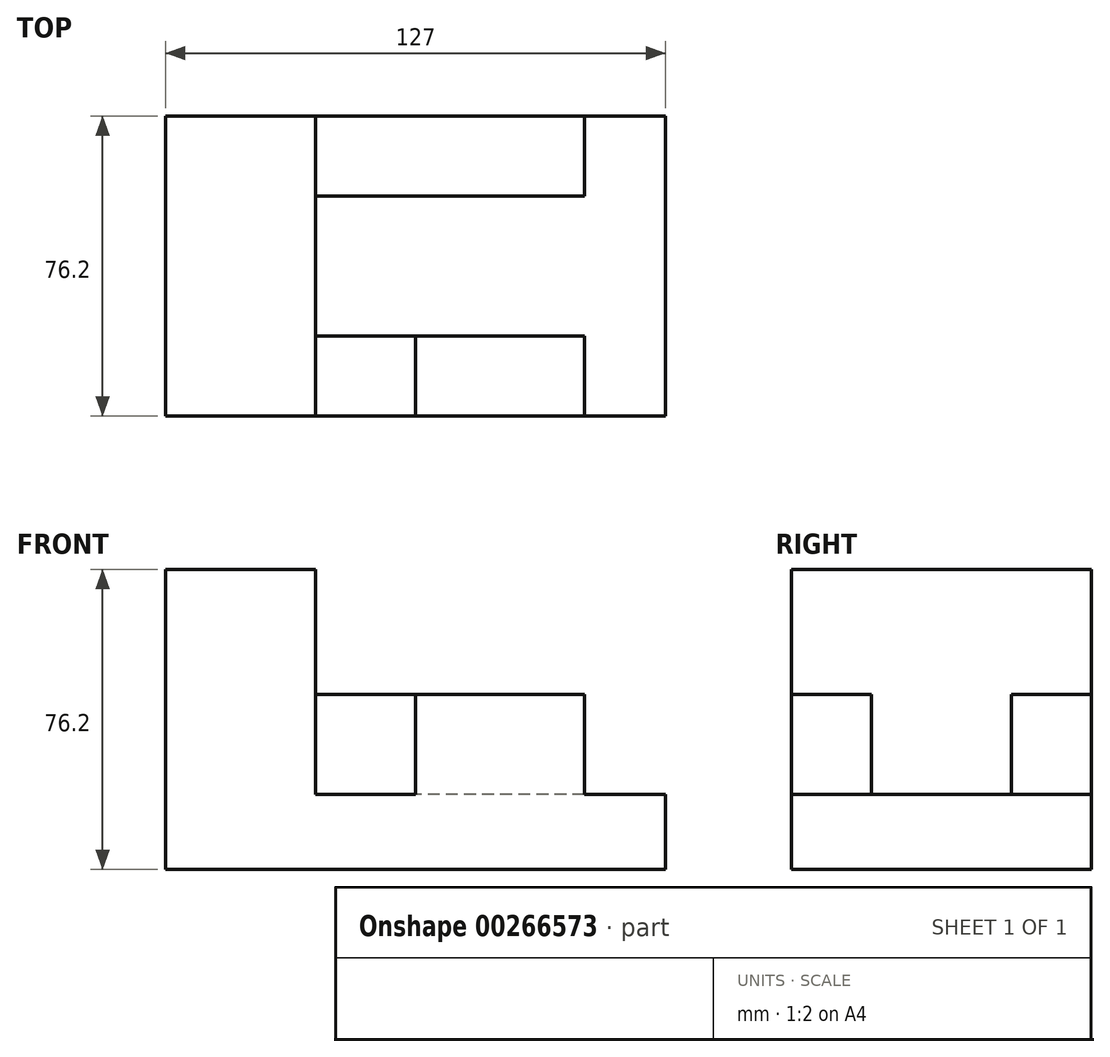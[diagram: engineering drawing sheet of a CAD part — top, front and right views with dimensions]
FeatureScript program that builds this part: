
annotation { "Feature Type Name" : "Feature", "Feature Type Description" : "" }
export const myFeature = defineFeature(function(context is Context, id is Id, definition is map)
    precondition{}
    {
        {
            var Q0;
            Q0=qCreatedBy(makeId("Top.planeOp"),FACE);
            var sketch = newSketch(context, id + "F0", { "sketchPlane" : qUnion([Q0])});
            skLineSegment(sketch, "E0.bottom", {"start": v(63.5, 38.1) * mm, "end": v(-63.5, 38.1) * mm});
            skLineSegment(sketch, "E0.top", {"start": v(63.5, -38.1) * mm, "end": v(-63.5, -38.1) * mm});
            skLineSegment(sketch, "E0.left", {"start": v(63.5, 38.1) * mm, "end": v(63.5, -38.1) * mm});
            skLineSegment(sketch, "E0.right", {"start": v(-63.5, 38.1) * mm, "end": v(-63.5, -38.1) * mm});
            skPoint(sketch, "E0.middle", {"position": v(0, 0) * mm});
            skSolve(sketch);
        }
        {
            var Q0;
            Q0=makeQuery(id+"F0.imprint","IMPRINT",FACE,{"disambiguationData":[TD([[makeQuery(id+"F0.imprint","IMPRINT",EDGE,{"derivedFrom":sQuery(id+"F0.wireOp",EDGE,"E0.bottom")}),1.0]])]});
            extrude(context, id + "F1", {"entities" : qUnion([Q0]), "depth" : 76.2 * mm});
        }
        {
            var Q0;
            Q0=qCreatedBy(makeId("Front.planeOp"),FACE);
            var sketch = newSketch(context, id + "F2", { "sketchPlane" : qUnion([Q0])});
            skLineSegment(sketch, "E1.bottom", {"start": v(-25.4, 87.45) * mm, "end": v(126.35, 87.45) * mm});
            skLineSegment(sketch, "E1.top", {"start": v(-25.4, 19.05) * mm, "end": v(126.35, 19.05) * mm});
            skLineSegment(sketch, "E1.left", {"start": v(-25.4, 87.45) * mm, "end": v(-25.4, 19.05) * mm});
            skLineSegment(sketch, "E1.right", {"start": v(126.35, 87.45) * mm, "end": v(126.35, 19.05) * mm});
            skSolve(sketch);
        }
        {
            var Q0;
            Q0=makeQuery(id+"F2.imprint","IMPRINT",FACE,{"disambiguationData":[TD([[makeQuery(id+"F2.imprint","IMPRINT",EDGE,{"derivedFrom":sQuery(id+"F2.wireOp",EDGE,"E1.bottom")}),-1.0]])]});
            extrude(context, id + "F3", {"entities" : qUnion([Q0]), "operationType" : NewBodyOperationType.REMOVE, "endBound" : BoundingType.SYMMETRIC, "oppositeDirection" : true, "depth" : 118.36 * mm});
        }
        {
            var Q0;
            Q0=qCreatedBy(makeId("Right.planeOp"),FACE);
            var sketch = newSketch(context, id + "F4", { "sketchPlane" : qUnion([Q0])});
            skLineSegment(sketch, "E2.bottom", {"start": v(-38.1, 44.45) * mm, "end": v(-17.78, 44.45) * mm});
            skLineSegment(sketch, "E2.top", {"start": v(-38.1, 19.05) * mm, "end": v(-17.78, 19.05) * mm});
            skLineSegment(sketch, "E2.left", {"start": v(-38.1, 44.45) * mm, "end": v(-38.1, 19.05) * mm});
            skLineSegment(sketch, "E2.right", {"start": v(-17.78, 44.45) * mm, "end": v(-17.78, 19.05) * mm});
            skSolve(sketch);
        }
        {
            var Q0;
            Q0 = qSketchRegion(id + "F4", true);
            var Q1;
            Q1=makeQuery(id+"F1.opExtrude","SWEPT_FACE",FACE,{"disambiguationData":[OSD([sQuery(id+"F0.wireOp",EDGE,"E0.left")])]});
            extrude(context, id + "F5", {"entities" : qUnion([Q0]), "operationType" : NewBodyOperationType.ADD, "endBoundEntityFace" : qUnion([Q1]), "depth" : 42.93 * mm});
        }
        {
            var Q0;
            Q0=makeQuery(id+"F5.opExtrude","CAP_FACE",FACE,{"disambiguationData":[OSD([sQuery(id+"F4.wireOp",EDGE,"E2.bottom"),sQuery(id+"F4.wireOp",EDGE,"E2.top"),sQuery(id+"F4.wireOp",EDGE,"E2.left"),sQuery(id+"F4.wireOp",EDGE,"E2.right")])],"isStart":true});
            var Q1;
            Q1=makeQuery(id+"F3.boolean.opBoolean","COPY",FACE,{"derivedFrom":makeQuery(id+"F3.opExtrude","SWEPT_FACE",FACE,{"disambiguationData":[OSD([sQuery(id+"F2.wireOp",EDGE,"E1.left")])]})});
            extrude(context, id + "F6", {"entities" : qUnion([Q0]), "endBound" : BoundingType.UP_TO_SURFACE, "endBoundEntityFace" : qUnion([Q1]), "depth" : 25.4 * mm});
        }
        {
            var Q0;
            Q0=qCreatedBy(makeId("Right.planeOp"),FACE);
            var sketch = newSketch(context, id + "F7", { "sketchPlane" : qUnion([Q0])});
            skLineSegment(sketch, "E3.bottom", {"start": v(17.78, 44.45) * mm, "end": v(38.1, 44.45) * mm});
            skLineSegment(sketch, "E3.top", {"start": v(17.78, 19.05) * mm, "end": v(38.1, 19.05) * mm});
            skLineSegment(sketch, "E3.left", {"start": v(17.78, 44.45) * mm, "end": v(17.78, 19.05) * mm});
            skLineSegment(sketch, "E3.right", {"start": v(38.1, 44.45) * mm, "end": v(38.1, 19.05) * mm});
            skSolve(sketch);
        }
        {
            var Q0;
            Q0=makeQuery(id+"F7.imprint","IMPRINT",FACE,{"disambiguationData":[TD([[makeQuery(id+"F7.imprint","IMPRINT",EDGE,{"derivedFrom":sQuery(id+"F7.wireOp",EDGE,"E3.bottom")}),-1.0]])]});
            var Q1;
            {var subQ0=sQuery(id+"F0.wireOp",EDGE,"E0.left");Q1=makeQuery(id+"F5.boolean.opBoolean","MERGE",FACE,{"derivedFrom":[makeQuery(id+"F1.opExtrude","SWEPT_FACE",FACE,{"disambiguationData":[OSD([subQ0])]}),makeQuery(id+"F5.opExtrude","CAP_FACE",FACE,{"disambiguationData":[OSD([subQ0])],"isStart":false})]});}
            extrude(context, id + "F8", {"entities" : qUnion([Q0]), "operationType" : NewBodyOperationType.ADD, "endBoundEntityFace" : qUnion([Q1]), "depth" : 42.93 * mm});
        }
        {
            var Q0;
            Q0=makeQuery(id+"F8.opExtrude","CAP_FACE",FACE,{"disambiguationData":[OSD([sQuery(id+"F7.wireOp",EDGE,"E3.bottom"),sQuery(id+"F7.wireOp",EDGE,"E3.top"),sQuery(id+"F7.wireOp",EDGE,"E3.left"),sQuery(id+"F7.wireOp",EDGE,"E3.right")])],"isStart":true});
            var Q1;
            Q1=makeQuery(id+"F3.boolean.opBoolean","COPY",FACE,{"derivedFrom":makeQuery(id+"F3.opExtrude","SWEPT_FACE",FACE,{"disambiguationData":[OSD([sQuery(id+"F2.wireOp",EDGE,"E1.left")])]})});
            extrude(context, id + "F9", {"entities" : qUnion([Q0]), "operationType" : NewBodyOperationType.ADD, "endBound" : BoundingType.UP_TO_SURFACE, "endBoundEntityFace" : qUnion([Q1]), "depth" : 25.4 * mm});
        }
    });
